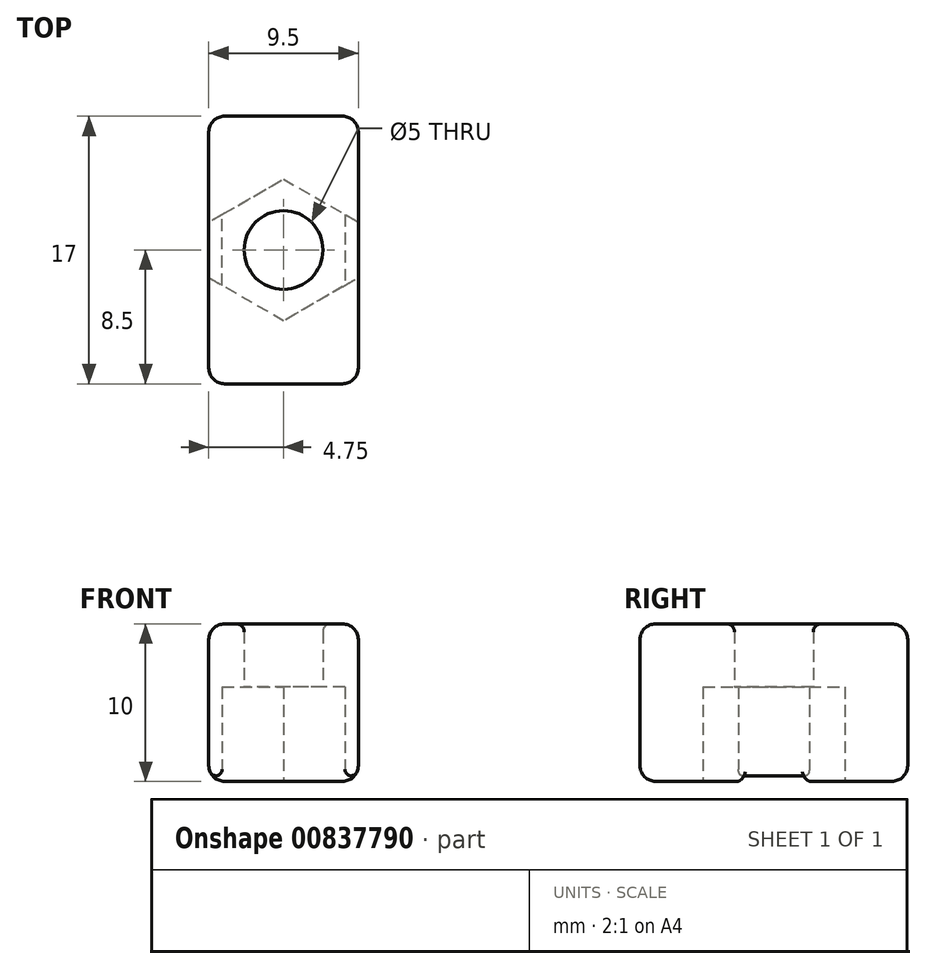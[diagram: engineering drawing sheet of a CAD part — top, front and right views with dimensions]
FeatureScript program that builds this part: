
annotation { "Feature Type Name" : "Feature", "Feature Type Description" : "" }
export const myFeature = defineFeature(function(context is Context, id is Id, definition is map)
    precondition{}
    {
        {
            var Q0;
            Q0=qCreatedBy(makeId("Top.planeOp"),FACE);
            var sketch = newSketch(context, id + "F0", { "sketchPlane" : qUnion([Q0])});
            skLineSegment(sketch, "E0.bottom", {"start": v(4.75, 8.5) * mm, "end": v(-4.75, 8.5) * mm});
            skLineSegment(sketch, "E0.top", {"start": v(4.75, -8.5) * mm, "end": v(-4.75, -8.5) * mm});
            skLineSegment(sketch, "E0.left", {"start": v(4.75, 8.5) * mm, "end": v(4.75, -8.5) * mm});
            skLineSegment(sketch, "E0.right", {"start": v(-4.75, 8.5) * mm, "end": v(-4.75, -8.5) * mm});
            skPoint(sketch, "E0.middle", {"position": v(0, 0) * mm});
            skCircle(sketch, "E1", {"center": v(0, 0) * mm, "radius": 2.5 * mm});
            skLineSegment(sketch, "E2", {"start": v(0, 0) * mm, "end": v(0, 2.5) * mm, "construction": true});
            skLineSegment(sketch, "E3", {"start": v(0, 0) * mm, "end": v(2.17, 1.25) * mm, "construction": true});
            skLineSegment(sketch, "E4", {"start": v(0, 0) * mm, "end": v(2.17, -1.25) * mm, "construction": true});
            skLineSegment(sketch, "E5", {"start": v(0, 0) * mm, "end": v(-2.17, 1.25) * mm, "construction": true});
            skLineSegment(sketch, "E6", {"start": v(0, 0) * mm, "end": v(-2.17, -1.25) * mm, "construction": true});
            skLineSegment(sketch, "E7", {"start": v(0, 0) * mm, "end": v(0, -2.5) * mm, "construction": true});
            skLineSegment(sketch, "E8", {"start": v(0, 2.5) * mm, "end": v(0, 4.5) * mm, "construction": true});
            skLineSegment(sketch, "E9", {"start": v(0, 4.5) * mm, "end": v(4.75, 4.5) * mm, "construction": true});
            skLineSegment(sketch, "E10", {"start": v(0, 4.5) * mm, "end": v(-4.75, 4.5) * mm, "construction": true});
            skLineSegment(sketch, "E11", {"start": v(0, -2.5) * mm, "end": v(0, -4.5) * mm, "construction": true});
            skLineSegment(sketch, "E12", {"start": v(0, -4.5) * mm, "end": v(4.75, -4.5) * mm, "construction": true});
            skLineSegment(sketch, "E13", {"start": v(0, -4.5) * mm, "end": v(-4.75, -4.5) * mm, "construction": true});
            skLineSegment(sketch, "E14", {"start": v(2.17, 1.25) * mm, "end": v(3.9, 2.25) * mm, "construction": true});
            skLineSegment(sketch, "E15", {"start": v(2.17, -1.25) * mm, "end": v(3.9, -2.25) * mm, "construction": true});
            skLineSegment(sketch, "E16", {"start": v(-2.17, -1.25) * mm, "end": v(-3.9, -2.25) * mm, "construction": true});
            skLineSegment(sketch, "E17", {"start": v(-2.17, 1.25) * mm, "end": v(-3.9, 2.25) * mm, "construction": true});
            skLineSegment(sketch, "E18", {"start": v(-3.9, 2.25) * mm, "end": v(0, 4.5) * mm});
            skLineSegment(sketch, "E19", {"start": v(0, 4.5) * mm, "end": v(3.9, 2.25) * mm});
            skLineSegment(sketch, "E20", {"start": v(3.9, 2.25) * mm, "end": v(3.9, -2.25) * mm});
            skLineSegment(sketch, "E21", {"start": v(3.9, -2.25) * mm, "end": v(0, -4.5) * mm});
            skLineSegment(sketch, "E22", {"start": v(0, -4.5) * mm, "end": v(-3.9, -2.25) * mm});
            skLineSegment(sketch, "E23", {"start": v(-3.9, -2.25) * mm, "end": v(-3.9, 2.25) * mm});
            skSolve(sketch);
        }
        {
            var Q0;
            Q0 = qSketchRegion(id + "F0", true);
            var Q1;
            Q1=makeQuery(id+"F0.imprint","IMPRINT",FACE,{"disambiguationData":[TD([[makeQuery(id+"F0.imprint","IMPRINT",EDGE,{"derivedFrom":sQuery(id+"F0.wireOp",EDGE,"E1")}),-1.0]])]});
            extrude(context, id + "F1", {"entities" : qUnion([Q0, Q1]), "depth" : 10 * mm, "offsetDistance" : 25 * mm});
        }
        {
            var Q0;
            Q0=makeQuery(id+"F0.imprint","IMPRINT",FACE,{"disambiguationData":[TD([[makeQuery(id+"F0.imprint","IMPRINT",EDGE,{"derivedFrom":sQuery(id+"F0.wireOp",EDGE,"E1")}),-1.0]])]});
            extrude(context, id + "F2", {"entities" : qUnion([Q0]), "operationType" : NewBodyOperationType.REMOVE, "depth" : 6 * mm, "offsetDistance" : 25 * mm});
        }
        {
            var Q0;
            Q0=makeQuery(id+"F1.opExtrude","SWEPT_FACE",FACE,{"disambiguationData":[OSD([sQuery(id+"F0.wireOp",EDGE,"E0.bottom")])]});
            var Q1;
            Q1=makeQuery(id+"F1.opExtrude","SWEPT_FACE",FACE,{"disambiguationData":[OSD([sQuery(id+"F0.wireOp",EDGE,"E0.top")])]});
            var Q2;
            Q2=makeQuery(id+"F1.opExtrude","SWEPT_FACE",FACE,{"disambiguationData":[OSD([sQuery(id+"F0.wireOp",EDGE,"E0.right")])]});
            var Q3;
            Q3=makeQuery(id+"F1.opExtrude","SWEPT_FACE",FACE,{"disambiguationData":[OSD([sQuery(id+"F0.wireOp",EDGE,"E0.left")])]});
            fillet(context, id + "F3", {"entities" : qUnion([Q0, Q1, Q2, Q3]), "radius" : 1 * mm, "tangentPropagation" : true, "allowEdgeOverflow" : false});
        }
        {
            var Q0;
            Q0=makeQuery(id+"F3.opFillet","BLEND_EDGE",EDGE,{"blendedFrom":[makeQuery(id+"F1.opExtrude","CAP_EDGE",EDGE,{"disambiguationData":[OSD([sQuery(id+"F0.wireOp",EDGE,"E0.right")])],"isStart":true}),makeQuery(id+"F2.boolean.opBoolean","COPY",FACE,{"derivedFrom":makeQuery(id+"F2.opExtrude","SWEPT_FACE",FACE,{"disambiguationData":[OSD([sQuery(id+"F0.wireOp",EDGE,"E23")])]})})],"blendedInto":[makeQuery(id+"F2.boolean.opBoolean","COPY",FACE,{"derivedFrom":makeQuery(id+"F2.opExtrude","SWEPT_FACE",FACE,{"disambiguationData":[OSD([sQuery(id+"F0.wireOp",EDGE,"E23")])]})})]});
            var Q1;
            Q1=makeQuery(id+"F2.boolean.opBoolean","COPY",EDGE,{"derivedFrom":makeQuery(id+"F2.opExtrude","CAP_EDGE",EDGE,{"disambiguationData":[OSD([sQuery(id+"F0.wireOp",EDGE,"E18")])],"isStart":true})});
            var Q2;
            Q2=makeQuery(id+"F2.boolean.opBoolean","COPY",EDGE,{"derivedFrom":makeQuery(id+"F2.opExtrude","CAP_EDGE",EDGE,{"disambiguationData":[OSD([sQuery(id+"F0.wireOp",EDGE,"E19")])],"isStart":true})});
            var Q3;
            Q3=makeQuery(id+"F3.opFillet","BLEND_EDGE",EDGE,{"blendedFrom":[makeQuery(id+"F1.opExtrude","CAP_EDGE",EDGE,{"disambiguationData":[OSD([sQuery(id+"F0.wireOp",EDGE,"E0.left")])],"isStart":true}),makeQuery(id+"F2.boolean.opBoolean","COPY",FACE,{"derivedFrom":makeQuery(id+"F2.opExtrude","SWEPT_FACE",FACE,{"disambiguationData":[OSD([sQuery(id+"F0.wireOp",EDGE,"E20")])]})})],"blendedInto":[makeQuery(id+"F2.boolean.opBoolean","COPY",FACE,{"derivedFrom":makeQuery(id+"F2.opExtrude","SWEPT_FACE",FACE,{"disambiguationData":[OSD([sQuery(id+"F0.wireOp",EDGE,"E20")])]})})]});
            var Q4;
            Q4=makeQuery(id+"F2.boolean.opBoolean","COPY",EDGE,{"derivedFrom":makeQuery(id+"F2.opExtrude","CAP_EDGE",EDGE,{"disambiguationData":[OSD([sQuery(id+"F0.wireOp",EDGE,"E21")])],"isStart":true})});
            var Q5;
            Q5=makeQuery(id+"F2.boolean.opBoolean","COPY",EDGE,{"derivedFrom":makeQuery(id+"F2.opExtrude","CAP_EDGE",EDGE,{"disambiguationData":[OSD([sQuery(id+"F0.wireOp",EDGE,"E22")])],"isStart":true})});
            fillet(context, id + "F4", {"entities" : qUnion([Q0, Q1, Q2, Q3, Q4, Q5]), "radius" : .4 * mm, "tangentPropagation" : true, "allowEdgeOverflow" : false});
        }
        {
            var Q0;
            Q0=makeQuery(id+"F2.boolean.opBoolean","COPY",EDGE,{"derivedFrom":makeQuery(id+"F2.opExtrude","CAP_EDGE",EDGE,{"disambiguationData":[OSD([sQuery(id+"F0.wireOp",EDGE,"E1")])],"isStart":false})});
            var Q1;
            Q1=makeQuery(id+"F1.opExtrude","CAP_EDGE",EDGE,{"disambiguationData":[OSD([sQuery(id+"F0.wireOp",EDGE,"E1")])],"isStart":false});
            fillet(context, id + "F5", {"entities" : qUnion([Q0, Q1]), "radius" : .5 * mm, "tangentPropagation" : true, "allowEdgeOverflow" : false});
        }
    });
